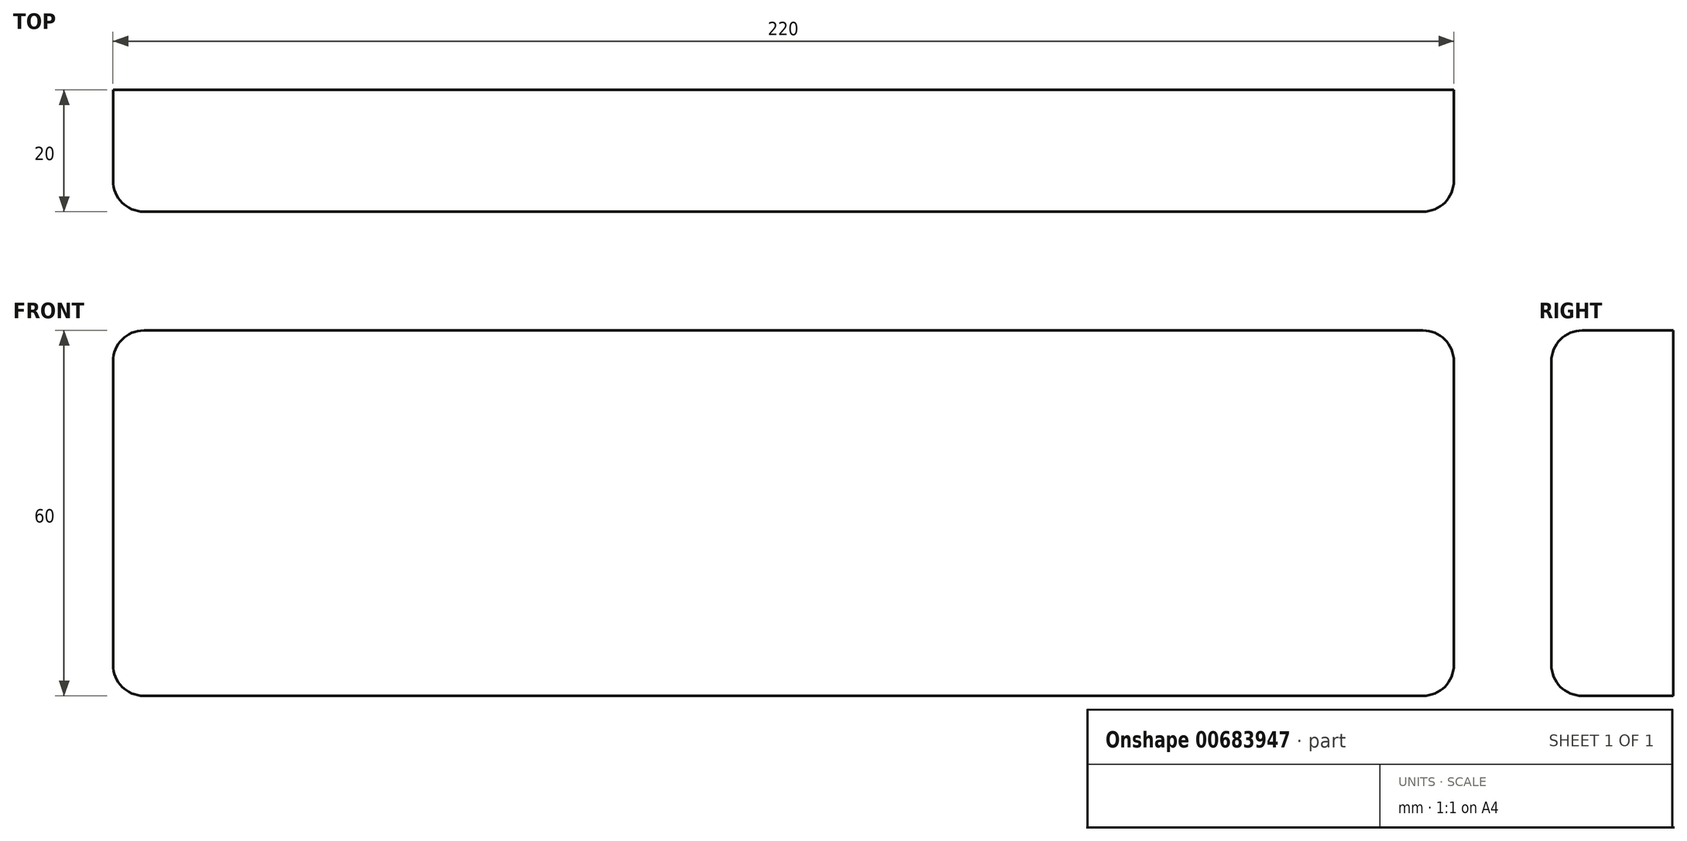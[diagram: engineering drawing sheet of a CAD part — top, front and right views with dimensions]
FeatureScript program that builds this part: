
annotation { "Feature Type Name" : "Feature", "Feature Type Description" : "" }
export const myFeature = defineFeature(function(context is Context, id is Id, definition is map)
    precondition{}
    {
        {
            var Q0;
            Q0=qCreatedBy(makeId("Front.planeOp"),FACE);
            var sketch = newSketch(context, id + "F0", { "sketchPlane" : qUnion([Q0])});
            skLineSegment(sketch, "E0.bottom", {"start": v(-109.72, -2.67) * mm, "end": v(110.28, -2.67) * mm});
            skLineSegment(sketch, "E0.top", {"start": v(-109.72, -62.67) * mm, "end": v(110.28, -62.67) * mm});
            skLineSegment(sketch, "E0.left", {"start": v(-109.72, -2.67) * mm, "end": v(-109.72, -62.67) * mm});
            skLineSegment(sketch, "E0.right", {"start": v(110.28, -2.67) * mm, "end": v(110.28, -62.67) * mm});
            skSolve(sketch);
        }
        {
            var Q0;
            Q0=makeQuery(id+"F0.imprint","IMPRINT",FACE,{"disambiguationData":[TD([[makeQuery(id+"F0.imprint","IMPRINT",EDGE,{"derivedFrom":sQuery(id+"F0.wireOp",EDGE,"E0.bottom")}),-1.0]])]});
            extrude(context, id + "F1", {"entities" : qUnion([Q0]), "depth" : 20 * mm, "offsetDistance" : 25.4 * mm});
        }
        {
            var Q0;
            Q0=makeQuery(id+"F1.opExtrude","SWEPT_EDGE",EDGE,{"disambiguationData":[OSD([sQuery(id+"F0.wireOp",EDGE,"E0.top"),sQuery(id+"F0.wireOp",EDGE,"E0.left")])]});
            fillet(context, id + "F2", {"entities" : qUnion([Q0]), "radius" : 5.08 * mm, "tangentPropagation" : true, "allowEdgeOverflow" : false});
        }
        {
            var Q0;
            Q0=makeQuery(id+"F1.opExtrude","SWEPT_EDGE",EDGE,{"disambiguationData":[OSD([sQuery(id+"F0.wireOp",EDGE,"E0.bottom"),sQuery(id+"F0.wireOp",EDGE,"E0.left")])]});
            fillet(context, id + "F3", {"entities" : qUnion([Q0]), "radius" : 5.08 * mm, "tangentPropagation" : true, "allowEdgeOverflow" : false});
        }
        {
            var Q0;
            Q0=makeQuery(id+"F1.opExtrude","SWEPT_EDGE",EDGE,{"disambiguationData":[OSD([sQuery(id+"F0.wireOp",EDGE,"E0.bottom"),sQuery(id+"F0.wireOp",EDGE,"E0.right")])]});
            var Q1;
            Q1=makeQuery(id+"F1.opExtrude","SWEPT_EDGE",EDGE,{"disambiguationData":[OSD([sQuery(id+"F0.wireOp",EDGE,"E0.top"),sQuery(id+"F0.wireOp",EDGE,"E0.right")])]});
            fillet(context, id + "F4", {"entities" : qUnion([Q0, Q1]), "radius" : 5.08 * mm, "tangentPropagation" : true, "allowEdgeOverflow" : false});
        }
        {
            var Q0;
            Q0=makeQuery(id+"F1.opExtrude","CAP_EDGE",EDGE,{"disambiguationData":[OSD([sQuery(id+"F0.wireOp",EDGE,"E0.top")])],"isStart":false});
            fillet(context, id + "F5", {"entities" : qUnion([Q0]), "radius" : 5.08 * mm, "tangentPropagation" : true, "allowEdgeOverflow" : false});
        }
    });
